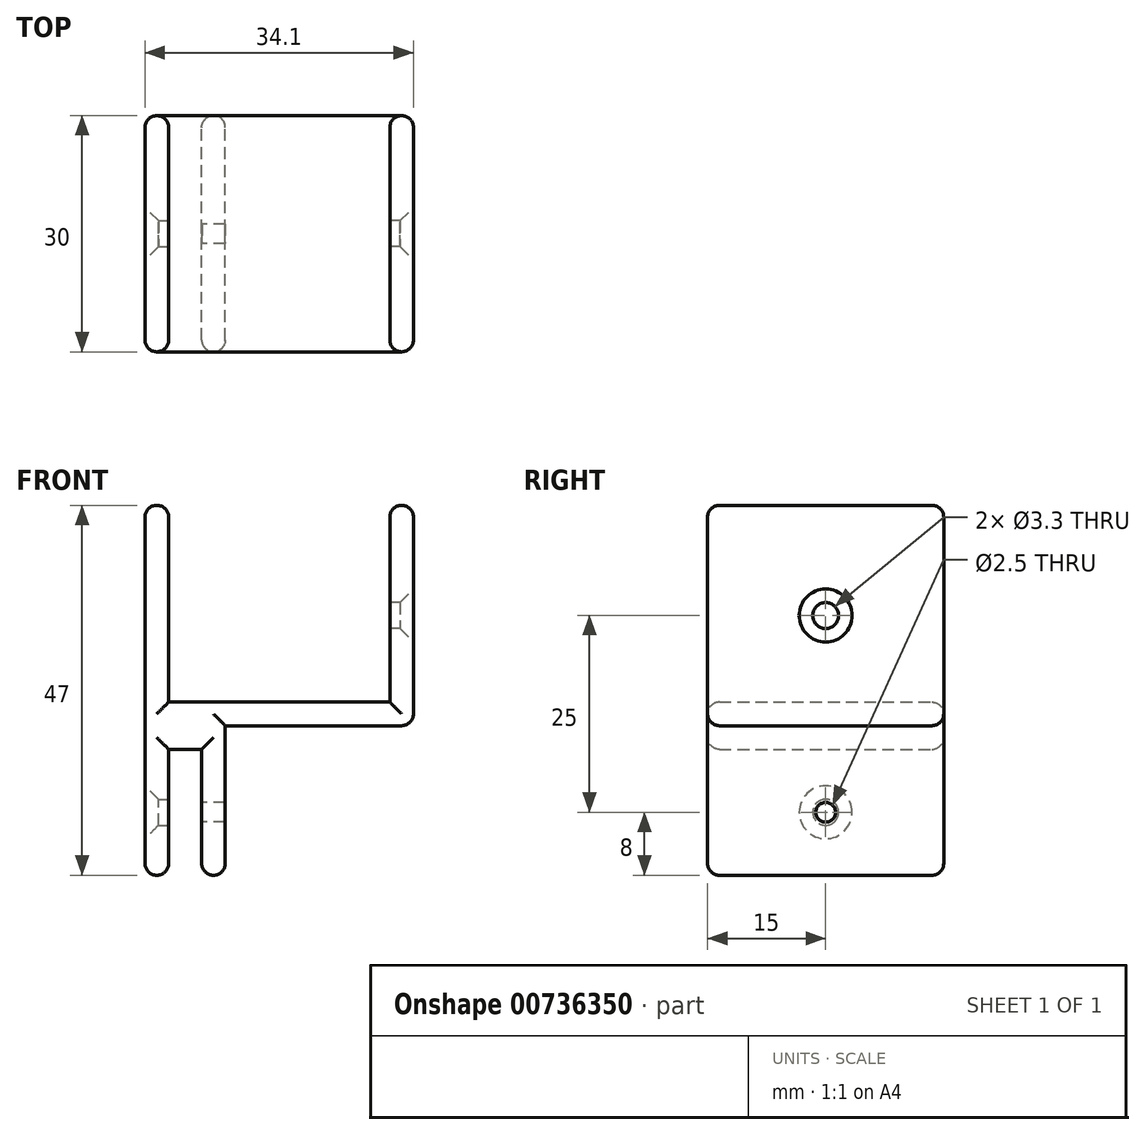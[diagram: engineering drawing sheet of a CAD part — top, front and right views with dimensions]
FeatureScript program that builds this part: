
annotation { "Feature Type Name" : "Feature", "Feature Type Description" : "" }
export const myFeature = defineFeature(function(context is Context, id is Id, definition is map)
    precondition{}
    {
        {
            var Q0;
            Q0=qCreatedBy(makeId("Front.planeOp"),FACE);
            var sketch = newSketch(context, id + "F0", { "sketchPlane" : qUnion([Q0])});
            skLineSegment(sketch, "E0", {"start": v(0, 0) * mm, "end": v(0, 28) * mm});
            skLineSegment(sketch, "E1", {"start": v(10.2, 0) * mm, "end": v(34.1, 0) * mm});
            skLineSegment(sketch, "E2", {"start": v(34.1, 0) * mm, "end": v(34.1, 28) * mm});
            skLineSegment(sketch, "E3.bottom", {"start": v(3, 3) * mm, "end": v(31.1, 3) * mm});
            skLineSegment(sketch, "E3.left", {"start": v(3, 3) * mm, "end": v(3, 28) * mm});
            skLineSegment(sketch, "E3.right", {"start": v(31.1, 3) * mm, "end": v(31.1, 28) * mm});
            skLineSegment(sketch, "E4", {"start": v(0, 28) * mm, "end": v(3, 28) * mm});
            skLineSegment(sketch, "E5", {"start": v(31.1, 28) * mm, "end": v(34.1, 28) * mm});
            skLineSegment(sketch, "E6", {"start": v(0, 0) * mm, "end": v(0, -19) * mm});
            skLineSegment(sketch, "E7", {"start": v(0, -19) * mm, "end": v(3, -19) * mm});
            skLineSegment(sketch, "E8", {"start": v(3, -19) * mm, "end": v(3, -3) * mm});
            skLineSegment(sketch, "E9", {"start": v(3, -3) * mm, "end": v(7.2, -3) * mm});
            skLineSegment(sketch, "E10", {"start": v(7.2, -3) * mm, "end": v(7.2, -19) * mm});
            skLineSegment(sketch, "E11", {"start": v(7.2, -19) * mm, "end": v(10.2, -19) * mm});
            skLineSegment(sketch, "E12", {"start": v(10.2, -19) * mm, "end": v(10.2, 0) * mm});
            skSolve(sketch);
        }
        {
            var Q0;
            Q0=makeQuery(id+"F0.imprint","IMPRINT",FACE,{"disambiguationData":[TD([[makeQuery(id+"F0.imprint","IMPRINT",EDGE,{"derivedFrom":sQuery(id+"F0.wireOp",EDGE,"E0")}),-1.0]])]});
            extrude(context, id + "F1", {"entities" : qUnion([Q0]), "depth" : 30 * mm, "offsetDistance" : 25 * mm});
        }
        {
            var Q0;
            Q0=makeQuery(id+"F1.opExtrude","SWEPT_FACE",FACE,{"disambiguationData":[OSD([sQuery(id+"F0.wireOp",EDGE,"E2")])]});
            var sketch = newSketch(context, id + "F2", { "sketchPlane" : qUnion([Q0])});
            skPoint(sketch, "E13", {"position": v(-15, 14) * mm});
            skSolve(sketch);
        }
        {
            var Q0;
            Q0=sQuery(id+"F2.wireOp",VERTEX,"E13");
            var Q1;
            Q1=makeQuery(id+"F1.opExtrude","SWEPT_BODY",BODY,{"disambiguationData":[OSD([sQuery(id+"F0.wireOp",EDGE,"E0"),sQuery(id+"F0.wireOp",EDGE,"E1"),sQuery(id+"F0.wireOp",EDGE,"E2"),sQuery(id+"F0.wireOp",EDGE,"E3.bottom"),sQuery(id+"F0.wireOp",EDGE,"E3.left"),sQuery(id+"F0.wireOp",EDGE,"E3.right"),sQuery(id+"F0.wireOp",EDGE,"E4"),sQuery(id+"F0.wireOp",EDGE,"E5"),sQuery(id+"F0.wireOp",EDGE,"E6"),sQuery(id+"F0.wireOp",EDGE,"E7"),sQuery(id+"F0.wireOp",EDGE,"E8"),sQuery(id+"F0.wireOp",EDGE,"E9"),sQuery(id+"F0.wireOp",EDGE,"E10"),sQuery(id+"F0.wireOp",EDGE,"E11"),sQuery(id+"F0.wireOp",EDGE,"E12")])]});
            hole(context, id + "F3", {"style" : HoleStyle.C_SINK, "endStyle" : HoleEndStyle.BLIND, "standardTappedOrClearance" : lookupTablePath({ "standard" : "ISO", "fit" : "Normal", "size" : "M3", "type" : "Clearance" }), "standardBlindInLast" : lookupTablePath({ "fit" : "Standard", "standard" : "ISO", "size" : "M3", "type" : "Clearance" }), "holeDiameter" : 3.3 * mm, "cSinkDiameter" : 6.72 * mm, "cSinkAngle" : 90 * degree, "majorDiameter" : 5 * mm, "holeDepth" : 13.5 * mm, "isTappedThrough" : true, "tappedDepth" : 12 * mm, "tapClearance" : 3, "startFromSketch" : true, "locations" : qUnion([Q0]), "scope" : qUnion([Q1])});
        }
        {
            var Q0;
            Q0=makeQuery(id+"F1.opExtrude","SWEPT_EDGE",EDGE,{"disambiguationData":[OSD([sQuery(id+"F0.wireOp",EDGE,"E6"),sQuery(id+"F0.wireOp",EDGE,"E7")])]});
            var Q1;
            Q1=makeQuery(id+"F1.opExtrude","SWEPT_EDGE",EDGE,{"disambiguationData":[OSD([sQuery(id+"F0.wireOp",EDGE,"E7"),sQuery(id+"F0.wireOp",EDGE,"E8")])]});
            var Q2;
            Q2=makeQuery(id+"F1.opExtrude","SWEPT_EDGE",EDGE,{"disambiguationData":[OSD([sQuery(id+"F0.wireOp",EDGE,"E10"),sQuery(id+"F0.wireOp",EDGE,"E11")])]});
            var Q3;
            Q3=makeQuery(id+"F1.opExtrude","SWEPT_EDGE",EDGE,{"disambiguationData":[OSD([sQuery(id+"F0.wireOp",EDGE,"E11"),sQuery(id+"F0.wireOp",EDGE,"E12")])]});
            var Q4;
            Q4=makeQuery(id+"F1.opExtrude","SWEPT_EDGE",EDGE,{"disambiguationData":[OSD([sQuery(id+"F0.wireOp",EDGE,"E3.right"),sQuery(id+"F0.wireOp",EDGE,"E5")])]});
            var Q5;
            Q5=makeQuery(id+"F1.opExtrude","SWEPT_EDGE",EDGE,{"disambiguationData":[OSD([sQuery(id+"F0.wireOp",EDGE,"E2"),sQuery(id+"F0.wireOp",EDGE,"E5")])]});
            var Q6;
            Q6=makeQuery(id+"F1.opExtrude","SWEPT_EDGE",EDGE,{"disambiguationData":[OSD([sQuery(id+"F0.wireOp",EDGE,"E3.left"),sQuery(id+"F0.wireOp",EDGE,"E4")])]});
            var Q7;
            Q7=makeQuery(id+"F1.opExtrude","SWEPT_EDGE",EDGE,{"disambiguationData":[OSD([sQuery(id+"F0.wireOp",EDGE,"E0"),sQuery(id+"F0.wireOp",EDGE,"E4")])]});
            var Q8;
            Q8=makeQuery(id+"F1.opExtrude","CAP_EDGE",EDGE,{"disambiguationData":[OSD([sQuery(id+"F0.wireOp",EDGE,"E4")])],"isStart":false});
            var Q9;
            Q9=makeQuery(id+"F1.opExtrude","CAP_EDGE",EDGE,{"disambiguationData":[OSD([sQuery(id+"F0.wireOp",EDGE,"E5")])],"isStart":false});
            var Q10;
            Q10=makeQuery(id+"F1.opExtrude","CAP_EDGE",EDGE,{"disambiguationData":[OSD([sQuery(id+"F0.wireOp",EDGE,"E3.right")])],"isStart":false});
            var Q11;
            Q11=makeQuery(id+"F1.opExtrude","CAP_EDGE",EDGE,{"disambiguationData":[OSD([sQuery(id+"F0.wireOp",EDGE,"E2")])],"isStart":false});
            var Q12;
            Q12=makeQuery(id+"F1.opExtrude","CAP_EDGE",EDGE,{"disambiguationData":[OSD([sQuery(id+"F0.wireOp",EDGE,"E3.left")])],"isStart":false});
            var Q13;
            Q13=makeQuery(id+"F1.opExtrude","CAP_EDGE",EDGE,{"disambiguationData":[OSD([sQuery(id+"F0.wireOp",EDGE,"E0"),sQuery(id+"F0.wireOp",EDGE,"E6")])],"isStart":false});
            var Q14;
            Q14=makeQuery(id+"F1.opExtrude","CAP_EDGE",EDGE,{"disambiguationData":[OSD([sQuery(id+"F0.wireOp",EDGE,"E3.bottom")])],"isStart":false});
            var Q15;
            Q15=makeQuery(id+"F1.opExtrude","CAP_EDGE",EDGE,{"disambiguationData":[OSD([sQuery(id+"F0.wireOp",EDGE,"E1")])],"isStart":false});
            var Q16;
            Q16=makeQuery(id+"F1.opExtrude","CAP_EDGE",EDGE,{"disambiguationData":[OSD([sQuery(id+"F0.wireOp",EDGE,"E12")])],"isStart":false});
            var Q17;
            Q17=makeQuery(id+"F1.opExtrude","CAP_EDGE",EDGE,{"disambiguationData":[OSD([sQuery(id+"F0.wireOp",EDGE,"E7")])],"isStart":false});
            var Q18;
            Q18=makeQuery(id+"F1.opExtrude","CAP_EDGE",EDGE,{"disambiguationData":[OSD([sQuery(id+"F0.wireOp",EDGE,"E11")])],"isStart":false});
            var Q19;
            Q19=makeQuery(id+"F1.opExtrude","CAP_EDGE",EDGE,{"disambiguationData":[OSD([sQuery(id+"F0.wireOp",EDGE,"E7")])],"isStart":true});
            var Q20;
            Q20=makeQuery(id+"F1.opExtrude","CAP_EDGE",EDGE,{"disambiguationData":[OSD([sQuery(id+"F0.wireOp",EDGE,"E11")])],"isStart":true});
            var Q21;
            Q21=makeQuery(id+"F1.opExtrude","CAP_EDGE",EDGE,{"disambiguationData":[OSD([sQuery(id+"F0.wireOp",EDGE,"E0"),sQuery(id+"F0.wireOp",EDGE,"E6")])],"isStart":true});
            var Q22;
            Q22=makeQuery(id+"F1.opExtrude","CAP_EDGE",EDGE,{"disambiguationData":[OSD([sQuery(id+"F0.wireOp",EDGE,"E8")])],"isStart":true});
            var Q23;
            Q23=makeQuery(id+"F1.opExtrude","CAP_EDGE",EDGE,{"disambiguationData":[OSD([sQuery(id+"F0.wireOp",EDGE,"E10")])],"isStart":true});
            var Q24;
            Q24=makeQuery(id+"F1.opExtrude","CAP_EDGE",EDGE,{"disambiguationData":[OSD([sQuery(id+"F0.wireOp",EDGE,"E12")])],"isStart":true});
            var Q25;
            Q25=makeQuery(id+"F1.opExtrude","CAP_EDGE",EDGE,{"disambiguationData":[OSD([sQuery(id+"F0.wireOp",EDGE,"E3.bottom")])],"isStart":true});
            var Q26;
            Q26=makeQuery(id+"F1.opExtrude","CAP_EDGE",EDGE,{"disambiguationData":[OSD([sQuery(id+"F0.wireOp",EDGE,"E3.left")])],"isStart":true});
            var Q27;
            Q27=makeQuery(id+"F1.opExtrude","CAP_EDGE",EDGE,{"disambiguationData":[OSD([sQuery(id+"F0.wireOp",EDGE,"E1")])],"isStart":true});
            var Q28;
            Q28=makeQuery(id+"F1.opExtrude","CAP_EDGE",EDGE,{"disambiguationData":[OSD([sQuery(id+"F0.wireOp",EDGE,"E2")])],"isStart":true});
            var Q29;
            Q29=makeQuery(id+"F1.opExtrude","SWEPT_EDGE",EDGE,{"disambiguationData":[OSD([sQuery(id+"F0.wireOp",EDGE,"E1"),sQuery(id+"F0.wireOp",EDGE,"E2")])]});
            var Q30;
            Q30=makeQuery(id+"F1.opExtrude","CAP_EDGE",EDGE,{"disambiguationData":[OSD([sQuery(id+"F0.wireOp",EDGE,"E9")])],"isStart":true});
            var Q31;
            Q31=makeQuery(id+"F1.opExtrude","CAP_EDGE",EDGE,{"disambiguationData":[OSD([sQuery(id+"F0.wireOp",EDGE,"E9")])],"isStart":false});
            var Q32;
            Q32=makeQuery(id+"F1.opExtrude","CAP_EDGE",EDGE,{"disambiguationData":[OSD([sQuery(id+"F0.wireOp",EDGE,"E5")])],"isStart":true});
            var Q33;
            Q33=makeQuery(id+"F1.opExtrude","CAP_EDGE",EDGE,{"disambiguationData":[OSD([sQuery(id+"F0.wireOp",EDGE,"E4")])],"isStart":true});
            var Q34;
            Q34=makeQuery(id+"F1.opExtrude","CAP_EDGE",EDGE,{"disambiguationData":[OSD([sQuery(id+"F0.wireOp",EDGE,"E3.right")])],"isStart":true});
            var Q35;
            Q35=makeQuery(id+"F1.opExtrude","CAP_EDGE",EDGE,{"disambiguationData":[OSD([sQuery(id+"F0.wireOp",EDGE,"E8")])],"isStart":false});
            var Q36;
            Q36=makeQuery(id+"F1.opExtrude","CAP_EDGE",EDGE,{"disambiguationData":[OSD([sQuery(id+"F0.wireOp",EDGE,"E10")])],"isStart":false});
            fillet(context, id + "F4", {"entities" : qUnion([Q0, Q1, Q2, Q3, Q4, Q5, Q6, Q7, Q8, Q9, Q10, Q11, Q12, Q13, Q14, Q15, Q16, Q17, Q18, Q19, Q20, Q21, Q22, Q23, Q24, Q25, Q26, Q27, Q28, Q29, Q30, Q31, Q32, Q33, Q34, Q35, Q36]), "radius" : 1.5 * mm, "tangentPropagation" : true, "allowEdgeOverflow" : false});
        }
        {
            var Q0;
            Q0=makeQuery(id+"F1.opExtrude","SWEPT_FACE",FACE,{"disambiguationData":[OSD([sQuery(id+"F0.wireOp",EDGE,"E0"),sQuery(id+"F0.wireOp",EDGE,"E6")])]});
            var sketch = newSketch(context, id + "F5", { "sketchPlane" : qUnion([Q0])});
            skPoint(sketch, "E14", {"position": v(15, -11) * mm});
            skSolve(sketch);
        }
        {
            var Q0;
            Q0=sQuery(id+"F5.wireOp",VERTEX,"E14");
            var Q1;
            Q1=makeQuery(id+"F1.opExtrude","SWEPT_BODY",BODY,{"disambiguationData":[OSD([sQuery(id+"F0.wireOp",EDGE,"E0"),sQuery(id+"F0.wireOp",EDGE,"E1"),sQuery(id+"F0.wireOp",EDGE,"E2"),sQuery(id+"F0.wireOp",EDGE,"E3.bottom"),sQuery(id+"F0.wireOp",EDGE,"E3.left"),sQuery(id+"F0.wireOp",EDGE,"E3.right"),sQuery(id+"F0.wireOp",EDGE,"E4"),sQuery(id+"F0.wireOp",EDGE,"E5"),sQuery(id+"F0.wireOp",EDGE,"E6"),sQuery(id+"F0.wireOp",EDGE,"E7"),sQuery(id+"F0.wireOp",EDGE,"E8"),sQuery(id+"F0.wireOp",EDGE,"E9"),sQuery(id+"F0.wireOp",EDGE,"E10"),sQuery(id+"F0.wireOp",EDGE,"E11"),sQuery(id+"F0.wireOp",EDGE,"E12")])]});
            hole(context, id + "F6", {"style" : HoleStyle.C_SINK, "endStyle" : HoleEndStyle.BLIND, "standardTappedOrClearance" : lookupTablePath({ "standard" : "ISO", "fit" : "Normal", "size" : "M3", "type" : "Clearance" }), "standardBlindInLast" : lookupTablePath({ "fit" : "Standard", "standard" : "ISO", "size" : "M3", "type" : "Clearance" }), "holeDiameter" : 3.3 * mm, "cSinkDiameter" : 6.72 * mm, "cSinkAngle" : 90 * degree, "majorDiameter" : 5 * mm, "holeDepth" : 7 * mm, "isTappedThrough" : true, "tappedDepth" : 12 * mm, "tapClearance" : 3, "startFromSketch" : true, "locations" : qUnion([Q0]), "scope" : qUnion([Q1])});
        }
        {
            var Q0;
            Q0=makeQuery(id+"F1.opExtrude","SWEPT_FACE",FACE,{"disambiguationData":[OSD([sQuery(id+"F0.wireOp",EDGE,"E12")])]});
            var sketch = newSketch(context, id + "F7", { "sketchPlane" : qUnion([Q0])});
            skPoint(sketch, "E15", {"position": v(-15, -11) * mm});
            skSolve(sketch);
        }
        {
            var Q0;
            Q0=sQuery(id+"F7.wireOp",VERTEX,"E15");
            var Q1;
            Q1=makeQuery(id+"F1.opExtrude","SWEPT_BODY",BODY,{"disambiguationData":[OSD([sQuery(id+"F0.wireOp",EDGE,"E0"),sQuery(id+"F0.wireOp",EDGE,"E1"),sQuery(id+"F0.wireOp",EDGE,"E2"),sQuery(id+"F0.wireOp",EDGE,"E3.bottom"),sQuery(id+"F0.wireOp",EDGE,"E3.left"),sQuery(id+"F0.wireOp",EDGE,"E3.right"),sQuery(id+"F0.wireOp",EDGE,"E4"),sQuery(id+"F0.wireOp",EDGE,"E5"),sQuery(id+"F0.wireOp",EDGE,"E6"),sQuery(id+"F0.wireOp",EDGE,"E7"),sQuery(id+"F0.wireOp",EDGE,"E8"),sQuery(id+"F0.wireOp",EDGE,"E9"),sQuery(id+"F0.wireOp",EDGE,"E10"),sQuery(id+"F0.wireOp",EDGE,"E11"),sQuery(id+"F0.wireOp",EDGE,"E12")])]});
            hole(context, id + "F8", {"style" : HoleStyle.SIMPLE, "endStyle" : HoleEndStyle.BLIND, "holeDiameter" : 2.5 * mm, "majorDiameter" : 5 * mm, "holeDepth" : 7 * mm, "isTappedThrough" : true, "tappedDepth" : 12 * mm, "tapClearance" : 3, "startFromSketch" : true, "locations" : qUnion([Q0]), "scope" : qUnion([Q1])});
        }
    });
